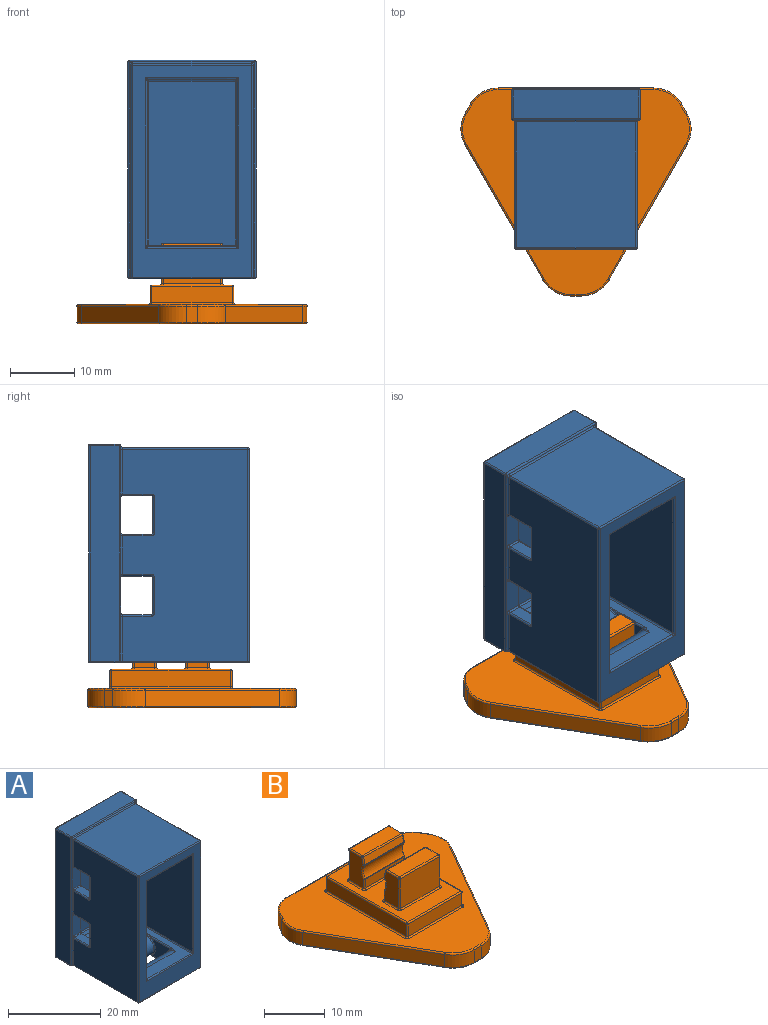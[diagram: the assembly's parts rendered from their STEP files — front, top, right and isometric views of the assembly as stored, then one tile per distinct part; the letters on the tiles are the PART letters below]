
ASSEMBLY  parts=2 mates=1
PART A: 221 faces, bbox 20x25x34.7 mm
  f0: cylinder r=2.5mm len=9.5mm, axis (-1,0,0), area 149.2mm2, adj f173,f181,f182,f193,f195,f196,f197,f205
  f1: plane 6.5x2.5mm, normal (0,-1,0), area 13.9mm2, adj f46,f66,f67,f76,f77,f104
  f2: plane 0.5x0.5mm, normal (0,-1,0), area 0.1mm2, adj f126,f127,f138
  f3: plane 6.5x2.5mm, normal (0,-1,0), area 13.9mm2, adj f52,f70,f71,f78,f79,f104
  f4: plane 6.5x2.5mm, normal (0,-1,0), area 13.9mm2, adj f95,f120,f121,f128,f129,f138
  f5: plane 6.5x2.5mm, normal (0,-1,0), area 13.9mm2, adj f138,f139,f144,f148,f152,f153
  f6: plane 25.5x22mm, normal (-1,0,0), area 489.9mm2, adj f39,f40,f41,f42,f43,f45,f46,f47
  f7: plane 25.5x22mm, normal (1,0,0), area 489.9mm2, adj f80,f81,f92,f94,f95,f96,f109,f110
  f8: plane 24.5x19.5mm, normal (0,0,-1), area 270.1mm2, adj f37,f38,f73,f75,f84,f100,f113,f124
  f9: plane 22x13.5mm, normal (0,0,1), area 109.2mm2, adj f37,f38,f160,f164,f167,f171,f175,f176
  f10: plane 0.5x0.5mm, normal (0,-1,0), area 0.1mm2, adj f104,f105,f126
  f11: plane 33x19.5mm, normal (-1,0,0), area 578.7mm2, adj f106,f108,f111,f112,f118,f119,f122,f130
  f12: plane 33x19.5mm, normal (1,0,0), area 578.7mm2, adj f55,f56,f57,f60,f61,f64,f65,f68
  f13: plane 22x13.5mm, normal (0,0,-1), area 297mm2, adj f157,f161,f165,f169
  f14: plane 19.5x18.5mm, normal (0,0,1), area 360.7mm2, adj f91,f98,f117,f118
  f15: plane 33x18.5mm, normal (0,-1,0), area 226.2mm2, adj f83,f98,f112,f113,f161,f162,f163,f164
  f16: plane 33.5x19.5mm, normal (0,1,0), area 653.3mm2, adj f72,f100,f101,f102
  f17: plane 19.5x4.5mm, normal (0,0,1), area 87.8mm2, adj f102,f103,f125,f126
  f18: plane 33.5x4.5mm, normal (1,0,0), area 150.8mm2, adj f72,f73,f103,f104
  f19: plane 33.5x4.5mm, normal (-1,0,0), area 150.8mm2, adj f101,f124,f125,f138
  f20: plane 5.5x2mm, normal (0,1,0), area 11mm2, adj f39,f44,f48,f55
  f21: plane 4.5x2mm, normal (0,0,1), area 9mm2, adj f44,f45,f65,f66
  f22: plane 4.5x2mm, normal (0,0,-1), area 9mm2, adj f47,f48,f67,f68
  f23: plane 4.5x2mm, normal (0,0,-1), area 9mm2, adj f53,f54,f71,f74
  f24: plane 5.5x2mm, normal (0,1,0), area 11mm2, adj f41,f50,f54,f56
  f25: plane 4.5x2mm, normal (0,0,1), area 9mm2, adj f50,f51,f69,f70
  f26: plane 4.5x2mm, normal (0,0,1), area 9mm2, adj f142,f151,f152,f156
  f27: plane 5.5x2mm, normal (0,1,0), area 11mm2, adj f140,f141,f150,f151
  f28: plane 4.5x2mm, normal (0,0,-1), area 9mm2, adj f135,f140,f144,f145
  f29: plane 5.5x2mm, normal (0,1,0), area 11mm2, adj f80,f93,f97,f106
  f30: plane 4.5x2mm, normal (0,0,-1), area 9mm2, adj f93,f94,f119,f120
  f31: plane 4.5x2mm, normal (0,0,1), area 9mm2, adj f96,f97,f121,f122
  f32: plane 25.5x13.5mm, normal (0,-1,0), area 344.2mm2, adj f157,f158,f159,f160
  f33: plane 5.84x4.5mm, normal (1,0,0), area 18.9mm2, adj f184,f189,f192,f193
  f34: plane 5.84x4.5mm, normal (-1,0,0), area 18.9mm2, adj f208,f213,f216,f217
  f35: plane 5.84x4.5mm, normal (-1,0,0), area 18.9mm2, adj f207,f214,f215,f220
  f36: plane 5.84x4.5mm, normal (1,0,0), area 18.9mm2, adj f183,f190,f191,f196
  f37: cylinder r=2.5mm len=9.5mm, axis (-1,0,0), area 74.6mm2, adj f8,f9,f184,f208
  f38: cylinder r=2.5mm len=9.5mm, axis (1,0,0), area 74.6mm2, adj f8,f9,f183,f207
  f39: cylinder r=0.25mm len=5.5mm, axis (0,0,1), area 2.2mm2, adj f6,f20,f40,f43
  f40: torus R=0.5mm, axis (-1,0,0), area 0.2mm2, adj f6,f39,f44,f45
  f41: cylinder r=0.25mm len=5.5mm, axis (0,0,1), area 2.2mm2, adj f6,f24,f42,f49
  f42: torus R=0.5mm, axis (-1,0,0), area 0.2mm2, adj f6,f41,f50,f51
  f43: torus R=0.5mm, axis (-1,0,0), area 0.2mm2, adj f6,f39,f47,f48
  f44: cylinder r=0.25mm len=2mm, axis (-1,0,0), area 0.8mm2, adj f20,f21,f40,f57
  f45: cylinder r=0.25mm len=4.5mm, axis (0,-1,0), area 1.8mm2, adj f6,f21,f40,f58
  f46: cylinder r=0.25mm len=5.5mm, axis (0,0,1), area 2.2mm2, adj f1,f6,f58,f59
  f47: cylinder r=0.25mm len=4.5mm, axis (0,1,0), area 1.8mm2, adj f6,f22,f43,f59
  f48: cylinder r=0.25mm len=2mm, axis (1,0,0), area 0.8mm2, adj f20,f22,f43,f60
  f49: torus R=0.5mm, axis (-1,0,0), area 0.2mm2, adj f6,f41,f53,f54
  f50: cylinder r=0.25mm len=2mm, axis (-1,0,0), area 0.8mm2, adj f24,f25,f42,f61
  f51: cylinder r=0.25mm len=4.5mm, axis (0,-1,0), area 1.8mm2, adj f6,f25,f42,f62
  f52: cylinder r=0.25mm len=5.5mm, axis (0,0,1), area 2.2mm2, adj f3,f6,f62,f63
  f53: cylinder r=0.25mm len=4.5mm, axis (0,1,0), area 1.8mm2, adj f6,f23,f49,f63
  f54: cylinder r=0.25mm len=2mm, axis (1,0,0), area 0.8mm2, adj f23,f24,f49,f64
  f55: cylinder r=0.25mm len=5.5mm, axis (0,0,-1), area 2.2mm2, adj f12,f20,f57,f60
  f56: cylinder r=0.25mm len=5.5mm, axis (0,0,-1), area 2.2mm2, adj f12,f24,f61,f64
  f57: torus R=0.5mm, axis (-1,0,0), area 0.2mm2, adj f12,f44,f55,f65
  f58: torus R=0.5mm, axis (-1,0,0), area 0.2mm2, adj f6,f45,f46,f66
  f59: torus R=0.5mm, axis (-1,0,0), area 0.2mm2, adj f6,f46,f47,f67
  f60: torus R=0.5mm, axis (-1,0,0), area 0.2mm2, adj f12,f48,f55,f68
  f61: torus R=0.5mm, axis (-1,0,0), area 0.2mm2, adj f12,f50,f56,f69
  f62: torus R=0.5mm, axis (-1,0,0), area 0.2mm2, adj f6,f51,f52,f70
  f63: torus R=0.5mm, axis (-1,0,0), area 0.2mm2, adj f6,f52,f53,f71
  f64: torus R=0.5mm, axis (-1,0,0), area 0.2mm2, adj f12,f54,f56,f74
  f65: cylinder r=0.25mm len=4.5mm, axis (0,1,0), area 1.8mm2, adj f12,f21,f57,f76
  f66: cylinder r=0.25mm len=2mm, axis (1,0,0), area 0.8mm2, adj f1,f21,f58,f76
  f67: cylinder r=0.25mm len=2mm, axis (-1,0,0), area 0.8mm2, adj f1,f22,f59,f77
  f68: cylinder r=0.25mm len=4.5mm, axis (0,-1,0), area 1.8mm2, adj f12,f22,f60,f77
  f69: cylinder r=0.25mm len=4.5mm, axis (0,1,0), area 1.8mm2, adj f12,f25,f61,f78
  f70: cylinder r=0.25mm len=2mm, axis (1,0,0), area 0.8mm2, adj f3,f25,f62,f78
  f71: cylinder r=0.25mm len=2mm, axis (-1,0,0), area 0.8mm2, adj f3,f23,f63,f79
  f72: cylinder r=0.25mm len=33.5mm, axis (0,0,-1), area 13.2mm2, adj f16,f18,f85,f86
  f73: cylinder r=0.25mm len=4.5mm, axis (0,1,0), area 1.8mm2, adj f8,f18,f85,f87
  f74: cylinder r=0.25mm len=4.5mm, axis (0,-1,0), area 1.8mm2, adj f12,f23,f64,f79
  f75: torus R=0.5mm, axis (0,0,1), area 0.2mm2, adj f8,f84,f87,f88
  f76: torus R=0.5mm, axis (0,-1,0), area 0.2mm2, adj f1,f65,f66,f88
  f77: torus R=0.5mm, axis (0,-1,0), area 0.2mm2, adj f1,f67,f68,f89
  f78: torus R=0.5mm, axis (0,-1,0), area 0.2mm2, adj f3,f69,f70,f89
  f79: torus R=0.5mm, axis (0,-1,0), area 0.2mm2, adj f3,f71,f74,f90
  f80: cylinder r=0.25mm len=5.5mm, axis (0,0,1), area 2.2mm2, adj f7,f29,f81,f92
  f81: torus R=0.5mm, axis (-1,0,0), area 0.2mm2, adj f7,f80,f93,f94
  f82: sphere r=0.25mm, area 0.1mm2, adj f83,f91,f98
  f83: cylinder r=0.25mm len=33mm, axis (0,0,-1), area 13mm2, adj f12,f15,f82,f99
  f84: cylinder r=0.25mm len=19.5mm, axis (0,1,0), area 7.7mm2, adj f8,f12,f75,f99
  f85: sphere r=0.25mm, area 0.1mm2, adj f72,f73,f100
  f86: sphere r=0.25mm, area 0.1mm2, adj f72,f102,f103
  f87: sphere r=0.25mm, area 0.1mm2, adj f73,f75,f104
  f88: cylinder r=0.25mm len=7mm, axis (0,0,1), area 2.7mm2, adj f12,f75,f76,f104
  f89: cylinder r=0.25mm len=6mm, axis (0,0,1), area 2.4mm2, adj f12,f77,f78,f104
  f90: cylinder r=0.25mm len=7mm, axis (0,0,1), area 2.7mm2, adj f12,f79,f104,f105
  f91: cylinder r=0.25mm len=19.5mm, axis (0,-1,0), area 7.7mm2, adj f12,f14,f82,f105
  f92: torus R=0.5mm, axis (-1,0,0), area 0.2mm2, adj f7,f80,f96,f97
  f93: cylinder r=0.25mm len=2mm, axis (-1,0,0), area 0.8mm2, adj f29,f30,f81,f108
  f94: cylinder r=0.25mm len=4.5mm, axis (0,1,0), area 1.8mm2, adj f7,f30,f81,f109
  f95: cylinder r=0.25mm len=5.5mm, axis (0,0,-1), area 2.2mm2, adj f4,f7,f109,f110
  f96: cylinder r=0.25mm len=4.5mm, axis (0,-1,0), area 1.8mm2, adj f7,f31,f92,f110
  f97: cylinder r=0.25mm len=2mm, axis (1,0,0), area 0.8mm2, adj f29,f31,f92,f111
  f98: cylinder r=0.25mm len=18.5mm, axis (1,0,0), area 7.3mm2, adj f14,f15,f82,f107
  f99: sphere r=0.25mm, area 0.1mm2, adj f83,f84,f113
  f100: cylinder r=0.25mm len=19.5mm, axis (1,0,0), area 7.7mm2, adj f8,f16,f85,f114
  f101: cylinder r=0.25mm len=33.5mm, axis (0,0,1), area 13.2mm2, adj f16,f19,f114,f115
  f102: cylinder r=0.25mm len=19.5mm, axis (1,0,0), area 7.7mm2, adj f16,f17,f86,f115
  f103: cylinder r=0.25mm len=4.5mm, axis (0,1,0), area 1.8mm2, adj f17,f18,f86,f116
  f104: cylinder r=0.25mm len=33.5mm, axis (0,0,1), area 13.2mm2, adj f1,f3,f10,f18,f87,f88,f89,f90
  f105: torus R=0.5mm, axis (0,-1,0), area 0.2mm2, adj f10,f90,f91,f117
  f106: cylinder r=0.25mm len=5.5mm, axis (0,0,-1), area 2.2mm2, adj f11,f29,f108,f111
  f107: sphere r=0.25mm, area 0.1mm2, adj f98,f112,f118
  f108: torus R=0.5mm, axis (-1,0,0), area 0.2mm2, adj f11,f93,f106,f119
  f109: torus R=0.5mm, axis (-1,0,0), area 0.2mm2, adj f7,f94,f95,f120
  f110: torus R=0.5mm, axis (-1,0,0), area 0.2mm2, adj f7,f95,f96,f121
  f111: torus R=0.5mm, axis (-1,0,0), area 0.2mm2, adj f11,f97,f106,f122
  f112: cylinder r=0.25mm len=33mm, axis (0,0,1), area 13mm2, adj f11,f15,f107,f123
  f113: cylinder r=0.25mm len=18.5mm, axis (-1,0,0), area 7.3mm2, adj f8,f15,f99,f123
  f114: sphere r=0.25mm, area 0.1mm2, adj f100,f101,f124
  f115: sphere r=0.25mm, area 0.1mm2, adj f101,f102,f125
  f116: sphere r=0.25mm, area 0.1mm2, adj f103,f104,f126
  f117: cylinder r=0.25mm len=18.5mm, axis (-1,0,0), area 7.3mm2, adj f14,f105,f126,f127
  f118: cylinder r=0.25mm len=19.5mm, axis (0,1,0), area 7.7mm2, adj f11,f14,f107,f127
  f119: cylinder r=0.25mm len=4.5mm, axis (0,-1,0), area 1.8mm2, adj f11,f30,f108,f128
  f120: cylinder r=0.25mm len=2mm, axis (-1,0,0), area 0.8mm2, adj f4,f30,f109,f128
  f121: cylinder r=0.25mm len=2mm, axis (1,0,0), area 0.8mm2, adj f4,f31,f110,f129
  f122: cylinder r=0.25mm len=4.5mm, axis (0,1,0), area 1.8mm2, adj f11,f31,f111,f129
  f123: sphere r=0.25mm, area 0.1mm2, adj f112,f113,f130
  f124: cylinder r=0.25mm len=4.5mm, axis (0,-1,0), area 1.8mm2, adj f8,f19,f114,f131
  f125: cylinder r=0.25mm len=4.5mm, axis (0,-1,0), area 1.8mm2, adj f17,f19,f115,f132
  f126: cylinder r=0.25mm len=19.5mm, axis (-1,0,0), area 7.7mm2, adj f2,f10,f17,f116,f117,f132
  f127: torus R=0.5mm, axis (0,-1,0), area 0.2mm2, adj f2,f117,f118,f133
  f128: torus R=0.5mm, axis (0,-1,0), area 0.2mm2, adj f4,f119,f120,f133
  f129: torus R=0.5mm, axis (0,-1,0), area 0.2mm2, adj f4,f121,f122,f134
  f130: cylinder r=0.25mm len=19.5mm, axis (0,-1,0), area 7.7mm2, adj f8,f11,f123,f137
  f131: sphere r=0.25mm, area 0.1mm2, adj f124,f137,f138
  f132: sphere r=0.25mm, area 0.1mm2, adj f125,f126,f138
  f133: cylinder r=0.25mm len=7mm, axis (0,0,-1), area 2.7mm2, adj f11,f127,f128,f138
  f134: cylinder r=0.25mm len=6mm, axis (0,0,-1), area 2.4mm2, adj f11,f129,f138,f139
  f135: cylinder r=0.25mm len=4.5mm, axis (0,-1,0), area 1.8mm2, adj f11,f28,f136,f139
  f136: torus R=0.5mm, axis (-1,0,0), area 0.2mm2, adj f11,f135,f140,f141
  f137: torus R=0.5mm, axis (0,0,1), area 0.2mm2, adj f8,f130,f131,f143
  f138: cylinder r=0.25mm len=33.5mm, axis (0,0,-1), area 13.2mm2, adj f2,f4,f5,f19,f131,f132,f133,f134
  f139: torus R=0.5mm, axis (0,-1,0), area 0.2mm2, adj f5,f134,f135,f144
  f140: cylinder r=0.25mm len=2mm, axis (-1,0,0), area 0.8mm2, adj f27,f28,f136,f146
  f141: cylinder r=0.25mm len=5.5mm, axis (0,0,-1), area 2.2mm2, adj f11,f27,f136,f147
  f142: cylinder r=0.25mm len=4.5mm, axis (0,1,0), area 1.8mm2, adj f11,f26,f147,f148
  f143: cylinder r=0.25mm len=7mm, axis (0,0,-1), area 2.7mm2, adj f11,f137,f138,f148
  f144: cylinder r=0.25mm len=2mm, axis (-1,0,0), area 0.8mm2, adj f5,f28,f139,f149
  f145: cylinder r=0.25mm len=4.5mm, axis (0,1,0), area 1.8mm2, adj f7,f28,f146,f149
  f146: torus R=0.5mm, axis (-1,0,0), area 0.2mm2, adj f7,f140,f145,f150
  f147: torus R=0.5mm, axis (-1,0,0), area 0.2mm2, adj f11,f141,f142,f151
  f148: torus R=0.5mm, axis (0,-1,0), area 0.2mm2, adj f5,f142,f143,f152
  f149: torus R=0.5mm, axis (-1,0,0), area 0.2mm2, adj f7,f144,f145,f153
  f150: cylinder r=0.25mm len=5.5mm, axis (0,0,1), area 2.2mm2, adj f7,f27,f146,f154
  f151: cylinder r=0.25mm len=2mm, axis (1,0,0), area 0.8mm2, adj f26,f27,f147,f154
  f152: cylinder r=0.25mm len=2mm, axis (1,0,0), area 0.8mm2, adj f5,f26,f148,f155
  f153: cylinder r=0.25mm len=5.5mm, axis (0,0,-1), area 2.2mm2, adj f5,f7,f149,f155
  f154: torus R=0.5mm, axis (-1,0,0), area 0.2mm2, adj f7,f150,f151,f156
  f155: torus R=0.5mm, axis (-1,0,0), area 0.2mm2, adj f7,f152,f153,f156
  f156: cylinder r=0.25mm len=4.5mm, axis (0,-1,0), area 1.8mm2, adj f7,f26,f154,f155
  f157: cylinder r=0.25mm len=13.85mm, axis (1,0,0), area 5.4mm2, adj f13,f32,f158,f159,f165,f169
  f158: cylinder r=0.25mm len=25.85mm, axis (0,0,1), area 10.1mm2, adj f7,f32,f157,f160,f169,f171
  f159: cylinder r=0.25mm len=25.85mm, axis (0,0,-1), area 10.1mm2, adj f6,f32,f157,f160,f165,f167
  f160: cylinder r=0.25mm len=13.85mm, axis (-1,0,0), area 5.4mm2, adj f9,f32,f158,f159,f167,f171
  f161: cylinder r=0.25mm len=14.5mm, axis (-1,0,0), area 5.5mm2, adj f13,f15,f166,f170
  f162: cylinder r=0.25mm len=26.5mm, axis (0,0,-1), area 10.2mm2, adj f7,f15,f170,f172
  f163: cylinder r=0.25mm len=26.5mm, axis (0,0,1), area 10.2mm2, adj f6,f15,f166,f168
  f164: cylinder r=0.25mm len=14.5mm, axis (1,0,0), area 5.5mm2, adj f9,f15,f168,f172
  f165: cylinder r=0.25mm len=22.18mm, axis (0,1,0), area 8.7mm2, adj f6,f13,f157,f159,f166
  f166: bspline ~0.5x0.5mm, area 0.1mm2, adj f161,f163,f165
  f167: cylinder r=0.25mm len=22.18mm, axis (0,-1,0), area 8.7mm2, adj f6,f9,f159,f160,f168
  f168: bspline ~0.5x0.5mm, area 0.1mm2, adj f163,f164,f167
  f169: cylinder r=0.25mm len=22.18mm, axis (0,-1,0), area 8.7mm2, adj f7,f13,f157,f158,f170
  f170: bspline ~0.5x0.5mm, area 0.1mm2, adj f161,f162,f169
  f171: cylinder r=0.25mm len=22.18mm, axis (0,1,0), area 8.7mm2, adj f7,f9,f158,f160,f172
  f172: bspline ~0.5x0.5mm, area 0.1mm2, adj f162,f164,f171
  f173: bspline ~1.46x0.45mm, area 0.3mm2, adj f0,f174,f193,f195
  f174: bspline ~1.58x0.38mm, area 0.3mm2, adj f173,f175,f192,f193
  f175: bspline ~1.58x0.26mm, area 0.3mm2, adj f9,f174,f176,f192
  f176: bspline ~1.58x0.26mm, area 0.3mm2, adj f9,f175,f177,f191
  f177: bspline ~1.58x0.38mm, area 0.3mm2, adj f176,f191,f195,f196
  f178: bspline ~1.58x0.26mm, area 0.3mm2, adj f8,f179,f190,f194
  f179: bspline ~1.58x0.26mm, area 0.3mm2, adj f8,f178,f180,f189
  f180: bspline ~1.58x0.38mm, area 0.3mm2, adj f179,f181,f189,f193
  f181: bspline ~1.46x0.45mm, area 0.3mm2, adj f0,f180,f182,f193
  f182: bspline ~1.46x0.45mm, area 0.3mm2, adj f0,f181,f194,f196
  f183: torus R=2.75mm, axis (-1,0,0), area 2.6mm2, adj f36,f38,f186,f187
  f184: torus R=2.75mm, axis (-1,0,0), area 2.6mm2, adj f33,f37,f185,f188
  f185: bspline ~1.65x0.5mm, area 0.2mm2, adj f8,f184,f189
  f186: bspline ~1.65x0.5mm, area 0.2mm2, adj f8,f183,f190
  f187: bspline ~1.65x0.5mm, area 0.2mm2, adj f9,f183,f191
  f188: bspline ~1.65x0.5mm, area 0.2mm2, adj f9,f184,f192
  f189: cylinder r=0.25mm len=5.86mm, axis (0,1,0), area 2.3mm2, adj f8,f33,f179,f180,f185
  f190: cylinder r=0.25mm len=5.86mm, axis (0,1,0), area 2.3mm2, adj f8,f36,f178,f186,f194
  f191: cylinder r=0.25mm len=5.86mm, axis (0,-1,0), area 2.3mm2, adj f9,f36,f176,f177,f187
  f192: cylinder r=0.25mm len=5.86mm, axis (0,-1,0), area 2.3mm2, adj f9,f33,f174,f175,f188
  f193: torus R=2.75mm, axis (-1,0,0), area 2mm2, adj f0,f33,f173,f174,f180,f181
  f194: bspline ~1.58x0.38mm, area 0.3mm2, adj f178,f182,f190,f196
  f195: bspline ~1.46x0.45mm, area 0.3mm2, adj f0,f173,f177,f196
  f196: torus R=2.75mm, axis (-1,0,0), area 2mm2, adj f0,f36,f177,f182,f194,f195
  f197: bspline ~1.46x0.45mm, area 0.3mm2, adj f0,f198,f217,f219
  f198: bspline ~1.58x0.38mm, area 0.3mm2, adj f197,f199,f216,f217
  f199: bspline ~1.58x0.26mm, area 0.3mm2, adj f8,f198,f200,f216
  f200: bspline ~1.58x0.26mm, area 0.3mm2, adj f8,f199,f201,f215
  f201: bspline ~1.58x0.38mm, area 0.3mm2, adj f200,f215,f219,f220
  f202: bspline ~1.58x0.26mm, area 0.3mm2, adj f9,f203,f214,f218
  f203: bspline ~1.58x0.26mm, area 0.3mm2, adj f9,f202,f204,f213
  f204: bspline ~1.58x0.38mm, area 0.3mm2, adj f203,f205,f213,f217
  f205: bspline ~1.46x0.45mm, area 0.3mm2, adj f0,f204,f206,f217
  f206: bspline ~1.46x0.45mm, area 0.3mm2, adj f0,f205,f218,f220
  f207: torus R=2.75mm, axis (-1,0,0), area 2.6mm2, adj f35,f38,f210,f211
  f208: torus R=2.75mm, axis (-1,0,0), area 2.6mm2, adj f34,f37,f209,f212
  f209: bspline ~1.65x0.5mm, area 0.2mm2, adj f9,f208,f213
  f210: bspline ~1.65x0.5mm, area 0.2mm2, adj f9,f207,f214
  f211: bspline ~1.65x0.5mm, area 0.2mm2, adj f8,f207,f215
  f212: bspline ~1.65x0.5mm, area 0.2mm2, adj f8,f208,f216
  f213: cylinder r=0.25mm len=5.86mm, axis (0,1,0), area 2.3mm2, adj f9,f34,f203,f204,f209
  f214: cylinder r=0.25mm len=5.86mm, axis (0,1,0), area 2.3mm2, adj f9,f35,f202,f210,f218
  f215: cylinder r=0.25mm len=5.86mm, axis (0,-1,0), area 2.3mm2, adj f8,f35,f200,f201,f211
  f216: cylinder r=0.25mm len=5.86mm, axis (0,-1,0), area 2.3mm2, adj f8,f34,f198,f199,f212
  f217: torus R=2.75mm, axis (-1,0,0), area 2mm2, adj f0,f34,f197,f198,f204,f205
  f218: bspline ~1.58x0.38mm, area 0.3mm2, adj f202,f206,f214,f220
  f219: bspline ~1.46x0.45mm, area 0.3mm2, adj f0,f197,f201,f220
  f220: torus R=2.75mm, axis (-1,0,0), area 2mm2, adj f0,f35,f201,f206,f218,f219
PART B: 137 faces, bbox 36.7x33.2x12.5 mm
  f0: plane 9x1.78mm, normal (0,-1,0), area 16mm2, adj f72,f81,f82,f86
  f1: plane 9x2.91mm, normal (0,0,1), area 26.1mm2, adj f57,f60,f64,f65
  f2: plane 9x1.78mm, normal (0,1,0), area 16mm2, adj f105,f110,f113,f116
  f3: plane 6x3.25mm, normal (1,0,0), area 18.5mm2, adj f90,f91,f100,f101,f110,f111
  f4: plane 6x3.25mm, normal (-1,0,0), area 18.5mm2, adj f93,f94,f103,f104,f112,f113
  f5: plane 2.5x1.4mm, normal (0.87,0.5,0), area 4mm2, adj f27,f32,f42,f55
  f6: plane 24.23x2.5mm, normal (0,1,0), area 60.6mm2, adj f27,f28,f43,f54
  f7: plane 2.5x1.4mm, normal (-0.87,0.5,0), area 4mm2, adj f28,f29,f39,f50
  f8: plane 20.98x12.11mm, normal (-0.87,-0.5,0), area 60.6mm2, adj f29,f30,f35,f46
  f9: plane 2.5x1.61mm, normal (0,-1,0), area 4mm2, adj f30,f31,f34,f47
  f10: plane 20.98x12.11mm, normal (0.87,-0.5,0), area 60.6mm2, adj f31,f32,f38,f51
  f11: plane 35.34x31.88mm, normal (0,0,1), area 498.9mm2, adj f33,f34,f35,f36,f37,f38,f39,f40
  f12: plane 35.34x31.88mm, normal (0,0,-1), area 762mm2, adj f45,f46,f47,f48,f49,f50,f51,f52
  f13: plane 18.5x12.5mm, normal (0,0,1), area 146.7mm2, adj f62,f67,f68,f71,f72,f73,f77,f78
  f14: plane 18.5x2.5mm, normal (1,0,0), area 46.2mm2, adj f120,f121,f130,f131
  f15: plane 12.5x2.5mm, normal (0,-1,0), area 31.2mm2, adj f117,f120,f124,f125
  f16: plane 18.5x2.5mm, normal (-1,0,0), area 46.2mm2, adj f123,f124,f132,f133
  f17: plane 12.5x2.5mm, normal (0,1,0), area 31.2mm2, adj f122,f131,f132,f136
  f18: plane 9x6mm, normal (0,1,0), area 54mm2, adj f57,f61,f62,f63
  f19: plane 6x3.25mm, normal (-1,0,0), area 18.5mm2, adj f63,f64,f73,f74,f82,f83
  f20: plane 6x3.25mm, normal (1,0,0), area 18.5mm2, adj f60,f61,f70,f71,f80,f81
  f21: plane 9x6mm, normal (0,-1,0), area 54mm2, adj f87,f90,f94,f95
  f22: plane 9x2.91mm, normal (0,0,1), area 26.1mm2, adj f87,f91,f92,f93
  f23: plane 9x1.31mm, normal (0,0.97,0.24), area 12.2mm2, adj f92,f101,f102,f103
  f24: plane 9x1.31mm, normal (0,-0.97,0.24), area 12.2mm2, adj f65,f70,f74,f75
  f25: cylinder r=2.65mm len=9mm, axis (1,0,0), area 25.1mm2, adj f75,f80,f83,f86
  f26: cylinder r=2.65mm len=9mm, axis (1,0,0), area 25.1mm2, adj f102,f111,f112,f116
  f27: cylinder r=5mm len=4.33mm, axis (0,0,-1), area 13.1mm2, adj f5,f6,f44,f56
  f28: cylinder r=5mm len=4.33mm, axis (0,0,-1), area 13.1mm2, adj f6,f7,f41,f52
  f29: cylinder r=5mm len=5mm, axis (0,0,-1), area 13.1mm2, adj f7,f8,f37,f48
  f30: cylinder r=5mm len=4.33mm, axis (0,0,-1), area 13.1mm2, adj f8,f9,f33,f45
  f31: cylinder r=5mm len=4.33mm, axis (0,0,-1), area 13.1mm2, adj f9,f10,f36,f49
  f32: cylinder r=5mm len=5mm, axis (0,0,-1), area 13.1mm2, adj f5,f10,f40,f53
  f33: torus R=4.75mm, axis (0,0,1), area 2mm2, adj f11,f30,f34,f35
  f34: cylinder r=0.25mm len=1.61mm, axis (-1,0,0), area 0.6mm2, adj f9,f11,f33,f36
  f35: cylinder r=0.25mm len=21.11mm, axis (-0.5,0.87,0), area 9.5mm2, adj f8,f11,f33,f37
  f36: torus R=4.75mm, axis (0,0,1), area 2mm2, adj f11,f31,f34,f38
  f37: torus R=4.75mm, axis (0,0,1), area 2mm2, adj f11,f29,f35,f39
  f38: cylinder r=0.25mm len=21.11mm, axis (-0.5,-0.87,0), area 9.5mm2, adj f10,f11,f36,f40
  f39: cylinder r=0.25mm len=1.52mm, axis (0.5,0.87,0), area 0.6mm2, adj f7,f11,f37,f41
  f40: torus R=4.75mm, axis (0,0,1), area 2mm2, adj f11,f32,f38,f42
  f41: torus R=4.75mm, axis (0,0,1), area 2mm2, adj f11,f28,f39,f43
  f42: cylinder r=0.25mm len=1.52mm, axis (0.5,-0.87,0), area 0.6mm2, adj f5,f11,f40,f44
  f43: cylinder r=0.25mm len=24.23mm, axis (1,0,0), area 9.5mm2, adj f6,f11,f41,f44
  f44: torus R=4.75mm, axis (0,0,1), area 2mm2, adj f11,f27,f42,f43
  f45: torus R=4.75mm, axis (0,0,1), area 2mm2, adj f12,f30,f46,f47
  f46: cylinder r=0.25mm len=21.11mm, axis (0.5,-0.87,0), area 9.5mm2, adj f8,f12,f45,f48
  f47: cylinder r=0.25mm len=1.61mm, axis (1,0,0), area 0.6mm2, adj f9,f12,f45,f49
  f48: torus R=4.75mm, axis (0,0,1), area 2mm2, adj f12,f29,f46,f50
  f49: torus R=4.75mm, axis (0,0,1), area 2mm2, adj f12,f31,f47,f51
  f50: cylinder r=0.25mm len=1.52mm, axis (-0.5,-0.87,0), area 0.6mm2, adj f7,f12,f48,f52
  f51: cylinder r=0.25mm len=21.11mm, axis (0.5,0.87,0), area 9.5mm2, adj f10,f12,f49,f53
  f52: torus R=4.75mm, axis (0,0,1), area 2mm2, adj f12,f28,f50,f54
  f53: torus R=4.75mm, axis (0,0,1), area 2mm2, adj f12,f32,f51,f55
  f54: cylinder r=0.25mm len=24.23mm, axis (-1,0,0), area 9.5mm2, adj f6,f12,f52,f56
  f55: cylinder r=0.25mm len=1.52mm, axis (-0.5,0.87,0), area 0.6mm2, adj f5,f12,f53,f56
  f56: torus R=4.75mm, axis (0,0,1), area 2mm2, adj f12,f27,f54,f55
  f57: cylinder r=0.25mm len=9mm, axis (1,0,0), area 3.5mm2, adj f1,f18,f58,f59
  f58: sphere r=0.25mm, area 0.1mm2, adj f57,f60,f61
  f59: sphere r=0.25mm, area 0.1mm2, adj f57,f63,f64
  f60: cylinder r=0.25mm len=2.91mm, axis (0,-1,0), area 1.1mm2, adj f1,f20,f58,f66
  f61: cylinder r=0.25mm len=6mm, axis (0,0,-1), area 2.4mm2, adj f18,f20,f58,f67
  f62: cylinder r=0.25mm len=9mm, axis (1,0,0), area 3.5mm2, adj f13,f18,f67,f68
  f63: cylinder r=0.25mm len=6mm, axis (0,0,1), area 2.4mm2, adj f18,f19,f59,f68
  f64: cylinder r=0.25mm len=2.91mm, axis (0,1,0), area 1.1mm2, adj f1,f19,f59,f69
  f65: cylinder r=0.25mm len=9mm, axis (-1,0,0), area 3mm2, adj f1,f24,f66,f69
  f66: sphere r=0.25mm, area 0.1mm2, adj f60,f65,f70
  f67: torus R=0.5mm, axis (0,0,1), area 0.2mm2, adj f13,f61,f62,f71
  f68: torus R=0.5mm, axis (0,0,1), area 0.2mm2, adj f13,f62,f63,f73
  f69: sphere r=0.25mm, area 0.1mm2, adj f64,f65,f74
  f70: cylinder r=0.25mm len=1.37mm, axis (0,-0.24,-0.97), area 0.5mm2, adj f20,f24,f66,f76
  f71: cylinder r=0.25mm len=3.25mm, axis (0,-1,0), area 1.3mm2, adj f13,f20,f67,f77
  f72: cylinder r=0.25mm len=9mm, axis (-1,0,0), area 3.5mm2, adj f0,f13,f77,f78
  f73: cylinder r=0.25mm len=3.25mm, axis (0,1,0), area 1.3mm2, adj f13,f19,f68,f78
  f74: cylinder r=0.25mm len=1.37mm, axis (0,0.24,0.97), area 0.5mm2, adj f19,f24,f69,f79
  f75: cylinder r=0.25mm len=9mm, axis (1,0,0), area 1.7mm2, adj f24,f25,f76,f79
  f76: sphere r=0.25mm, area 0mm2, adj f70,f75,f80
  f77: torus R=0.5mm, axis (0,0,1), area 0.2mm2, adj f13,f71,f72,f81
  f78: torus R=0.5mm, axis (0,0,1), area 0.2mm2, adj f13,f72,f73,f82
  f79: sphere r=0.25mm, area 0mm2, adj f74,f75,f83
  f80: torus R=2.9mm, axis (1,0,0), area 1.1mm2, adj f20,f25,f76,f84
  f81: cylinder r=0.25mm len=1.78mm, axis (0,0,1), area 0.7mm2, adj f0,f20,f77,f84
  f82: cylinder r=0.25mm len=1.78mm, axis (0,0,-1), area 0.7mm2, adj f0,f19,f78,f85
  f83: torus R=2.9mm, axis (1,0,0), area 1.1mm2, adj f19,f25,f79,f85
  f84: sphere r=0.25mm, area 0mm2, adj f80,f81,f86
  f85: sphere r=0.25mm, area 0mm2, adj f82,f83,f86
  f86: cylinder r=0.25mm len=9mm, axis (1,0,0), area 1.2mm2, adj f0,f25,f84,f85
  f87: cylinder r=0.25mm len=9mm, axis (-1,0,0), area 3.5mm2, adj f21,f22,f88,f89
  f88: sphere r=0.25mm, area 0.1mm2, adj f87,f90,f91
  f89: sphere r=0.25mm, area 0.1mm2, adj f87,f93,f94
  f90: cylinder r=0.25mm len=6mm, axis (0,0,1), area 2.4mm2, adj f3,f21,f88,f96
  f91: cylinder r=0.25mm len=2.91mm, axis (0,-1,0), area 1.1mm2, adj f3,f22,f88,f97
  f92: cylinder r=0.25mm len=9mm, axis (1,0,0), area 3mm2, adj f22,f23,f97,f98
  f93: cylinder r=0.25mm len=2.91mm, axis (0,1,0), area 1.1mm2, adj f4,f22,f89,f98
  f94: cylinder r=0.25mm len=6mm, axis (0,0,-1), area 2.4mm2, adj f4,f21,f89,f99
  f95: cylinder r=0.25mm len=9mm, axis (-1,0,0), area 3.5mm2, adj f13,f21,f96,f99
  f96: torus R=0.5mm, axis (0,0,1), area 0.2mm2, adj f13,f90,f95,f100
  f97: sphere r=0.25mm, area 0.1mm2, adj f91,f92,f101
  f98: sphere r=0.25mm, area 0.1mm2, adj f92,f93,f103
  f99: torus R=0.5mm, axis (0,0,1), area 0.2mm2, adj f13,f94,f95,f104
  f100: cylinder r=0.25mm len=3.25mm, axis (0,-1,0), area 1.3mm2, adj f3,f13,f96,f106
  f101: cylinder r=0.25mm len=1.37mm, axis (0,-0.24,0.97), area 0.5mm2, adj f3,f23,f97,f107
  f102: cylinder r=0.25mm len=9mm, axis (1,0,0), area 1.7mm2, adj f23,f26,f107,f108
  f103: cylinder r=0.25mm len=1.37mm, axis (0,0.24,-0.97), area 0.5mm2, adj f4,f23,f98,f108
  f104: cylinder r=0.25mm len=3.25mm, axis (0,1,0), area 1.3mm2, adj f4,f13,f99,f109
  f105: cylinder r=0.25mm len=9mm, axis (1,0,0), area 3.5mm2, adj f2,f13,f106,f109
  f106: torus R=0.5mm, axis (0,0,1), area 0.2mm2, adj f13,f100,f105,f110
  f107: sphere r=0.25mm, area 0mm2, adj f101,f102,f111
  f108: sphere r=0.25mm, area 0mm2, adj f102,f103,f112
  f109: torus R=0.5mm, axis (0,0,1), area 0.2mm2, adj f13,f104,f105,f113
  f110: cylinder r=0.25mm len=1.78mm, axis (0,0,-1), area 0.7mm2, adj f2,f3,f106,f114
  f111: torus R=2.9mm, axis (1,0,0), area 1.1mm2, adj f3,f26,f107,f114
  f112: torus R=2.9mm, axis (1,0,0), area 1.1mm2, adj f4,f26,f108,f115
  f113: cylinder r=0.25mm len=1.78mm, axis (0,0,1), area 0.7mm2, adj f2,f4,f109,f115
  f114: sphere r=0.25mm, area 0mm2, adj f110,f111,f116
  f115: sphere r=0.25mm, area 0mm2, adj f112,f113,f116
  f116: cylinder r=0.25mm len=9mm, axis (1,0,0), area 1.2mm2, adj f2,f26,f114,f115
  f117: cylinder r=0.25mm len=12.5mm, axis (-1,0,0), area 4.9mm2, adj f13,f15,f118,f119
  f118: sphere r=0.25mm, area 0.1mm2, adj f117,f120,f121
  f119: sphere r=0.25mm, area 0.1mm2, adj f117,f123,f124
  f120: cylinder r=0.25mm len=2.5mm, axis (0,0,1), area 1mm2, adj f14,f15,f118,f126
  f121: cylinder r=0.25mm len=18.5mm, axis (0,-1,0), area 7.3mm2, adj f13,f14,f118,f127
  f122: cylinder r=0.25mm len=12.5mm, axis (1,0,0), area 4.9mm2, adj f13,f17,f127,f128
  f123: cylinder r=0.25mm len=18.5mm, axis (0,1,0), area 7.3mm2, adj f13,f16,f119,f128
  f124: cylinder r=0.25mm len=2.5mm, axis (0,0,-1), area 1mm2, adj f15,f16,f119,f129
  f125: cylinder r=0.25mm len=12.5mm, axis (-1,0,0), area 4.9mm2, adj f11,f15,f126,f129
  f126: torus R=0.5mm, axis (0,0,1), area 0.2mm2, adj f11,f120,f125,f130
  f127: sphere r=0.25mm, area 0.1mm2, adj f121,f122,f131
  f128: sphere r=0.25mm, area 0.1mm2, adj f122,f123,f132
  f129: torus R=0.5mm, axis (0,0,1), area 0.2mm2, adj f11,f124,f125,f133
  f130: cylinder r=0.25mm len=18.5mm, axis (0,-1,0), area 7.3mm2, adj f11,f14,f126,f134
  f131: cylinder r=0.25mm len=2.5mm, axis (0,0,-1), area 1mm2, adj f14,f17,f127,f134
  f132: cylinder r=0.25mm len=2.5mm, axis (0,0,1), area 1mm2, adj f16,f17,f128,f135
  f133: cylinder r=0.25mm len=18.5mm, axis (0,1,0), area 7.3mm2, adj f11,f16,f129,f135
  f134: torus R=0.5mm, axis (0,0,1), area 0.2mm2, adj f11,f130,f131,f136
  f135: torus R=0.5mm, axis (0,0,1), area 0.2mm2, adj f11,f132,f133,f136
  f136: cylinder r=0.25mm len=12.5mm, axis (1,0,0), area 4.9mm2, adj f11,f17,f134,f135
PLACE A t=(0,7.82,6)mm
PLACE B t=(0,0,-1)mm
MATE revolute A.f0 <-> B.f25  axis (-1,0,0) through (-4.75,0,8.5)mm
